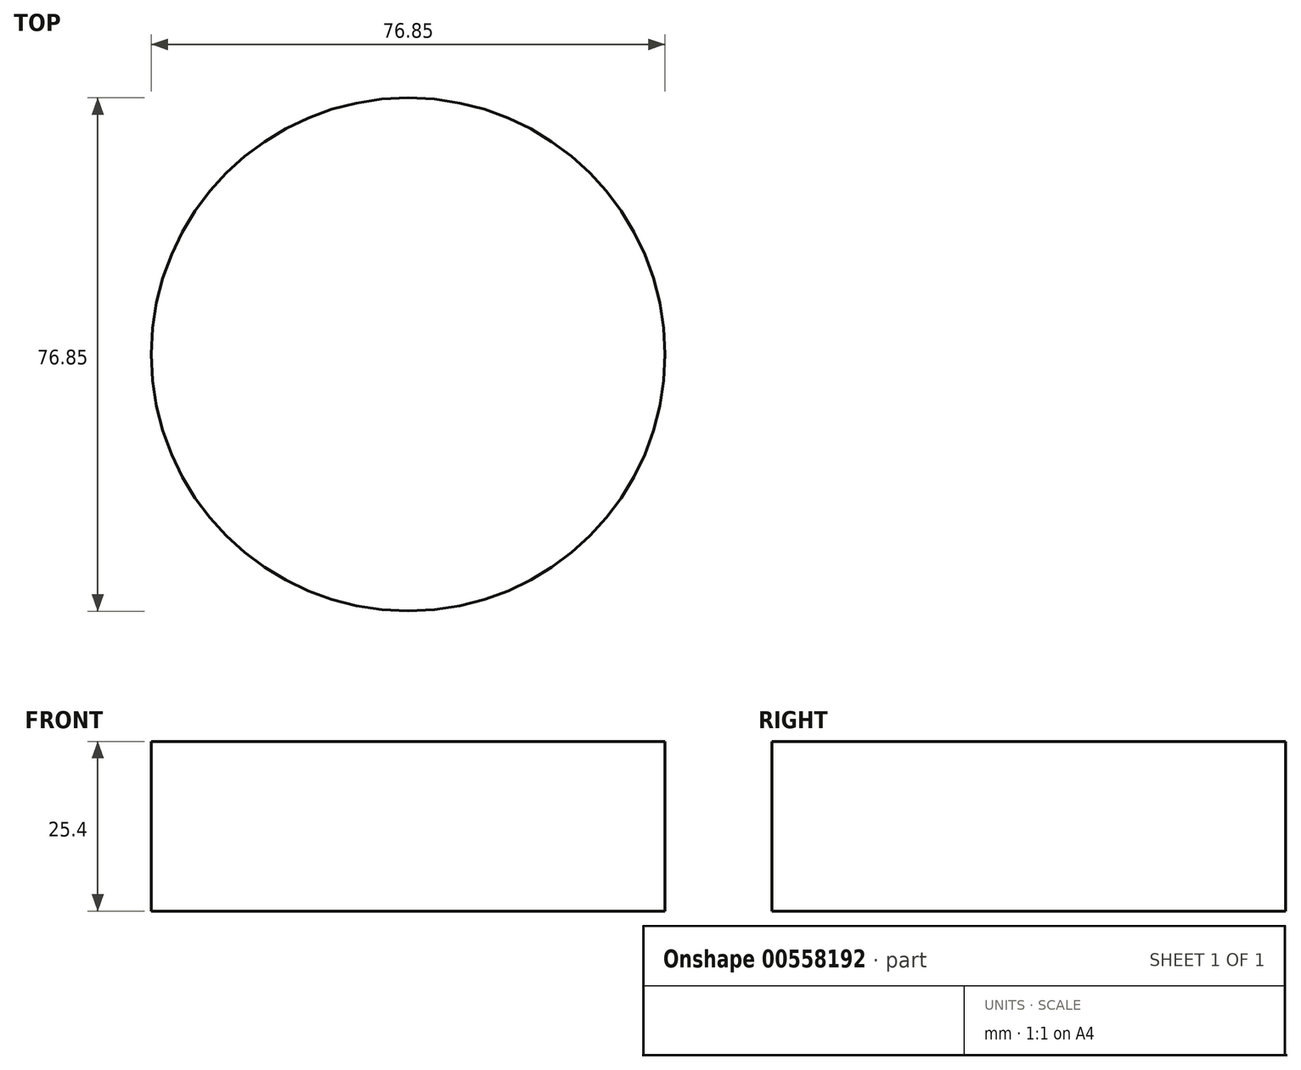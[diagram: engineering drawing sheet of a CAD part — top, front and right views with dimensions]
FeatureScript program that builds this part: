
annotation { "Feature Type Name" : "Feature", "Feature Type Description" : "" }
export const myFeature = defineFeature(function(context is Context, id is Id, definition is map)
    precondition{}
    {
        {
            var Q0;
            Q0=qCreatedBy(makeId("Top.planeOp"),FACE);
            var sketch = newSketch(context, id + "F0", { "sketchPlane" : qUnion([Q0])});
            skCircle(sketch, "E0", {"center": v(-27.14, 15.94) * mm, "radius": 38.42 * mm});
            skSolve(sketch);
        }
        {
            var Q0;
            Q0 = qSketchRegion(id + "F0", true);
            extrude(context, id + "F1", {"entities" : qUnion([Q0]), "oppositeDirection" : true, "depth" : 25.4 * mm, "offsetDistance" : 25.4 * mm});
        }
    });
